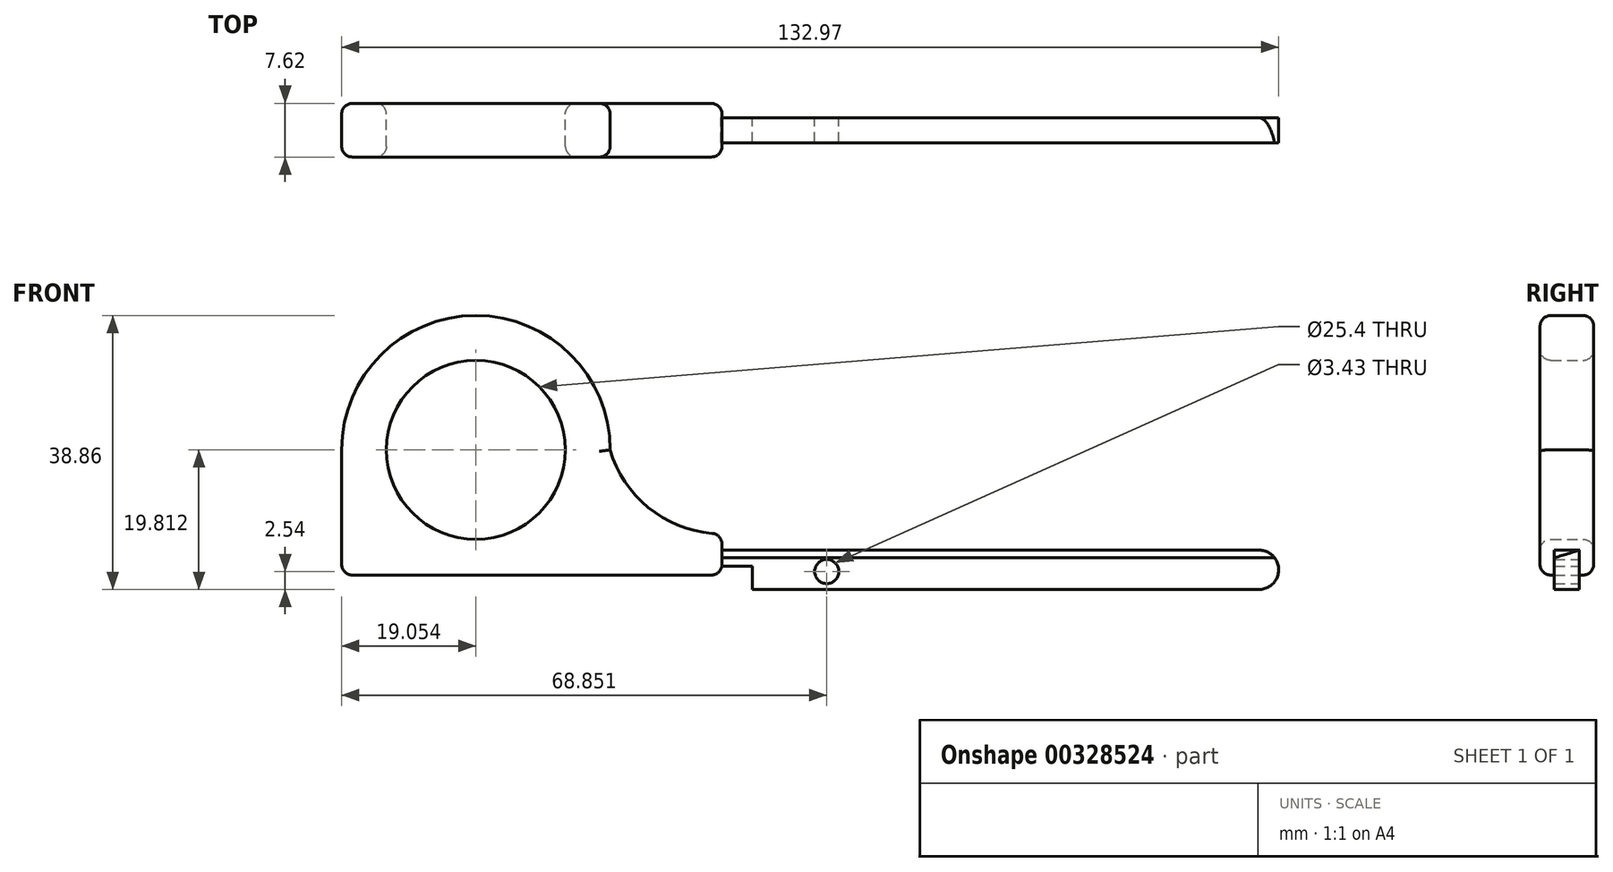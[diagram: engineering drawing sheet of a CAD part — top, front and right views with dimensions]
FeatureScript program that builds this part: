
annotation { "Feature Type Name" : "Feature", "Feature Type Description" : "" }
export const myFeature = defineFeature(function(context is Context, id is Id, definition is map)
    precondition{}
    {
        {
            var Q0;
            Q0=qCreatedBy(makeId("Front.planeOp"),FACE);
            var sketch = newSketch(context, id + "F0", { "sketchPlane" : qUnion([Q0])});
            skLineSegment(sketch, "E0", {"start": v(-53.86, -34.26) * mm, "end": v(-53.86, -16.48) * mm});
            skLineSegment(sketch, "E1", {"start": v(-53.86, -34.26) * mm, "end": v(0.12, -34.26) * mm});
            skLineSegment(sketch, "E2", {"start": v(0.12, -34.26) * mm, "end": v(0.12, -28.4) * mm});
            skLineSegment(sketch, "E3", {"start": v(0.12, -30.7) * mm, "end": v(76.32, -30.7) * mm});
            skArc(sketch, "E4", {"start": v(-15.76, -16.48) * mm, "mid": v(-34.8, 2.57) * mm, "end": v(-53.86, -16.48) * mm});
            skArc(sketch, "E5", {"start": v(-15.76, -16.48) * mm, "mid": v(-9.8, -25.09) * mm, "end": v(0.12, -28.4) * mm});
            skCircle(sketch, "E6", {"center": v(-34.8, -16.48) * mm, "radius": 12.7 * mm});
            skLineSegment(sketch, "E7", {"start": v(4.44, -32.99) * mm, "end": v(0.12, -32.99) * mm});
            skArc(sketch, "E8", {"start": v(76.32, -36.29) * mm, "mid": v(79.11, -33.5) * mm, "end": v(76.32, -30.7) * mm});
            skLineSegment(sketch, "E9", {"start": v(76.32, -36.29) * mm, "end": v(4.45, -36.29) * mm});
            skLineSegment(sketch, "E10", {"start": v(4.45, -36.29) * mm, "end": v(4.44, -32.99) * mm});
            skCircle(sketch, "E11", {"center": v(15, -33.75) * mm, "radius": 1.71 * mm});
            skSolve(sketch);
        }
        {
            var Q0;
            Q0=makeQuery(id+"F0.imprint","IMPRINT",FACE,{"disambiguationData":[TD([[makeQuery(id+"F0.imprint","IMPRINT",EDGE,{"derivedFrom":sQuery(id+"F0.wireOp",EDGE,"E0")}),-1.0]])]});
            extrude(context, id + "F1", {"entities" : qUnion([Q0]), "endBound" : BoundingType.SYMMETRIC, "depth" : 7.62 * mm});
        }
        {
            var Q0;
            {var subQ1=sQuery(id+"F0.wireOp",EDGE,"E3");Q0=makeQuery(id+"F0.imprint","IMPRINT",FACE,{"disambiguationData":[TD([[makeQuery(id+"F0.imprint","IMPRINT",EDGE,{"derivedFrom":subQ1}),-1.0]])]});}
            extrude(context, id + "F2", {"entities" : qUnion([Q0]), "operationType" : NewBodyOperationType.ADD, "endBound" : BoundingType.SYMMETRIC, "depth" : 3.56 * mm});
        }
        {
            var Q0;
            Q0=makeQuery(id+"F1.opExtrude","CAP_EDGE",EDGE,{"disambiguationData":[OSD([sQuery(id+"F0.wireOp",EDGE,"E6")])],"isStart":false});
            var Q1;
            Q1=makeQuery(id+"F1.opExtrude","CAP_EDGE",EDGE,{"disambiguationData":[OSD([sQuery(id+"F0.wireOp",EDGE,"E6")])],"isStart":true});
            var Q2;
            Q2=makeQuery(id+"F1.opExtrude","CAP_EDGE",EDGE,{"disambiguationData":[OSD([sQuery(id+"F0.wireOp",EDGE,"E0")])],"isStart":true});
            var Q3;
            Q3=makeQuery(id+"F1.opExtrude","CAP_EDGE",EDGE,{"disambiguationData":[OSD([sQuery(id+"F0.wireOp",EDGE,"E0")])],"isStart":false});
            var Q4;
            Q4=makeQuery(id+"F1.opExtrude","SWEPT_EDGE",EDGE,{"disambiguationData":[OSD([sQuery(id+"F0.wireOp",EDGE,"E0"),sQuery(id+"F0.wireOp",EDGE,"E1")])]});
            var Q5;
            Q5=makeQuery(id+"F1.opExtrude","CAP_EDGE",EDGE,{"disambiguationData":[OSD([sQuery(id+"F0.wireOp",EDGE,"E1")])],"isStart":false});
            var Q6;
            Q6=makeQuery(id+"F1.opExtrude","CAP_EDGE",EDGE,{"disambiguationData":[OSD([sQuery(id+"F0.wireOp",EDGE,"E1")])],"isStart":true});
            var Q7;
            Q7=makeQuery(id+"F1.opExtrude","CAP_EDGE",EDGE,{"disambiguationData":[OSD([sQuery(id+"F0.wireOp",EDGE,"E4")])],"isStart":false});
            var Q8;
            Q8=makeQuery(id+"F1.opExtrude","CAP_EDGE",EDGE,{"disambiguationData":[OSD([sQuery(id+"F0.wireOp",EDGE,"E4")])],"isStart":true});
            var Q9;
            Q9=makeQuery(id+"F1.opExtrude","CAP_EDGE",EDGE,{"disambiguationData":[OSD([sQuery(id+"F0.wireOp",EDGE,"E5")])],"isStart":true});
            var Q10;
            Q10=makeQuery(id+"F1.opExtrude","CAP_EDGE",EDGE,{"disambiguationData":[OSD([sQuery(id+"F0.wireOp",EDGE,"E5")])],"isStart":false});
            var Q11;
            Q11=makeQuery(id+"F1.opExtrude","CAP_EDGE",EDGE,{"disambiguationData":[OSD([sQuery(id+"F0.wireOp",EDGE,"E2")])],"isStart":false});
            var Q12;
            Q12=makeQuery(id+"F1.opExtrude","SWEPT_EDGE",EDGE,{"disambiguationData":[OSD([sQuery(id+"F0.wireOp",EDGE,"E2"),sQuery(id+"F0.wireOp",EDGE,"E5")])]});
            var Q13;
            Q13=makeQuery(id+"F1.opExtrude","CAP_EDGE",EDGE,{"disambiguationData":[OSD([sQuery(id+"F0.wireOp",EDGE,"E2")])],"isStart":true});
            var Q14;
            Q14=makeQuery(id+"F1.opExtrude","SWEPT_EDGE",EDGE,{"disambiguationData":[OSD([sQuery(id+"F0.wireOp",EDGE,"E1"),sQuery(id+"F0.wireOp",EDGE,"E2")])]});
            fillet(context, id + "F3", {"entities" : qUnion([Q0, Q1, Q2, Q3, Q4, Q5, Q6, Q7, Q8, Q9, Q10, Q11, Q12, Q13, Q14]), "radius" : 1.52 * mm, "tangentPropagation" : true, "allowEdgeOverflow" : false});
        }
        {
            var Q0;
            Q0=qCreatedBy(makeId("Right.planeOp"),FACE);
            var sketch = newSketch(context, id + "F4", { "sketchPlane" : qUnion([Q0])});
            skLineSegment(sketch, "E12", {"start": v(-1.8, -31.82) * mm, "end": v(1.82, -30.69) * mm});
            skLineSegment(sketch, "E13", {"start": v(1.82, -30.69) * mm, "end": v(-1.8, -30.69) * mm});
            skLineSegment(sketch, "E14", {"start": v(-1.8, -30.69) * mm, "end": v(-1.8, -31.82) * mm});
            skSolve(sketch);
        }
        {
            var Q0;
            Q0=makeQuery(id+"F4.imprint","IMPRINT",FACE,{"disambiguationData":[TD([[makeQuery(id+"F4.imprint","IMPRINT",EDGE,{"derivedFrom":sQuery(id+"F4.wireOp",EDGE,"E12")}),1.0]])]});
            extrude(context, id + "F5", {"entities" : qUnion([Q0]), "operationType" : NewBodyOperationType.REMOVE, "depth" : 99.57 * mm});
        }
    });
